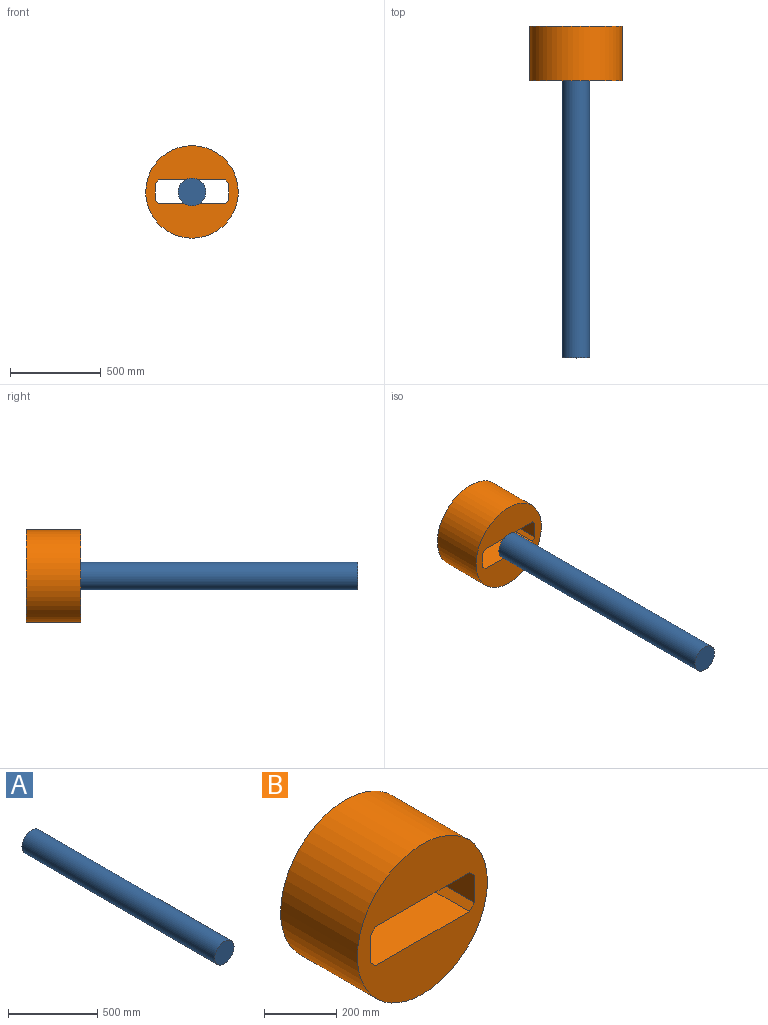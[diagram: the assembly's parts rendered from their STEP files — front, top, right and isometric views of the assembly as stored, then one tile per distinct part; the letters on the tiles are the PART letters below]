
ASSEMBLY  parts=2 mates=1
PART A: 3 faces, bbox 152.4x1524x152.4 mm
  f0: cylinder r=76.2mm len=1524mm, axis (0,1,0), area 729658.8mm2, adj f1,f2
  f1: plane 152.4x152.4mm, normal (0,-1,0), area 18241.5mm2, adj f0
  f2: plane 152.4x152.4mm, normal (0,1,0), area 18241.5mm2, adj f0
PART B: 11 faces, bbox 508x300x508 mm
  f0: plane 508x508mm, normal (0,-1,0), area 149876.3mm2, adj f2,f3,f4,f5,f6,f7,f8,f9
  f1: plane 508x508mm, normal (0,1,0), area 149876.3mm2, adj f2,f3,f4,f5,f6,f7,f8,f9
  f2: cylinder r=254mm len=508mm, axis (0,1,0), area 478778.7mm2, adj f0,f1
  f3: plane 300x91.91mm, normal (1,0,0), area 27571.9mm2, adj f0,f1,f8,f9
  f4: plane 366.4x300mm, normal (0,0,-1), area 109920mm2, adj f0,f1,f7,f8
  f5: plane 300x91.91mm, normal (-1,0,0), area 27571.9mm2, adj f0,f1,f7,f10
  f6: plane 366.4x300mm, normal (0,0,1), area 109920mm2, adj f0,f1,f9,f10
  f7: plane 300x20mm, normal (-0.71,0,-0.71), area 8485.3mm2, adj f0,f1,f4,f5
  f8: plane 300x20mm, normal (0.71,0,-0.71), area 8485.3mm2, adj f0,f1,f3,f4
  f9: plane 300x20mm, normal (0.71,0,0.71), area 8485.3mm2, adj f0,f1,f3,f6
  f10: plane 300x20mm, normal (-0.71,0,0.71), area 8485.3mm2, adj f0,f1,f5,f6
PLACE A t=(313.54,-769.22,-117.71)mm
PLACE B t=(313.54,-469.22,-117.71)mm
MATE fastened B.f2 <-> A.f0  axis (0,-1,0) through (313.54,-769.22,-117.71)mm
